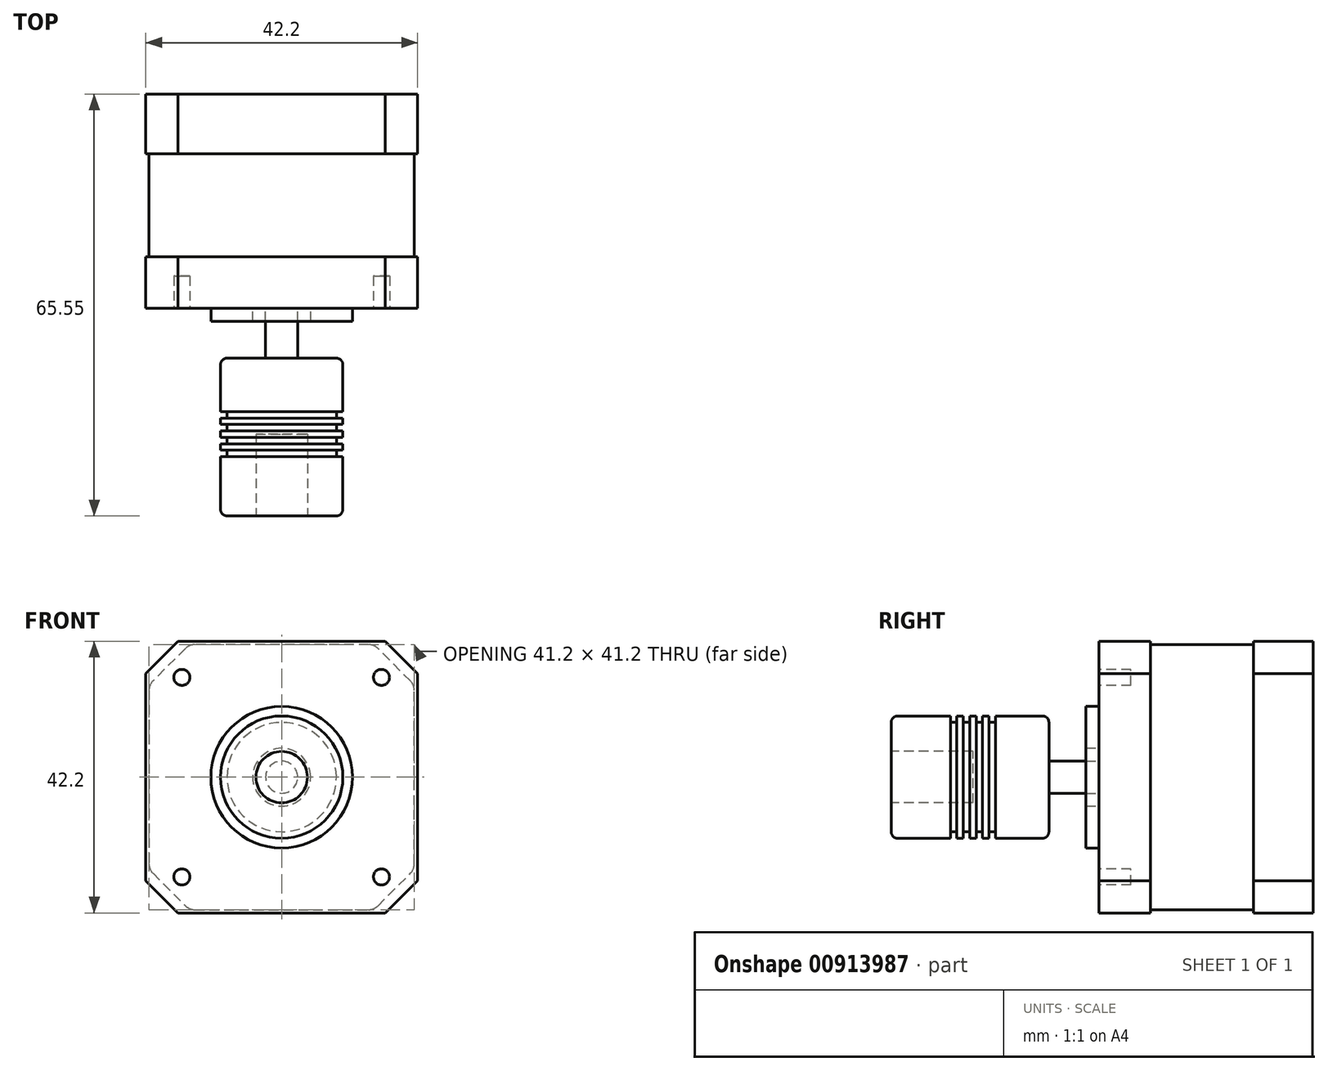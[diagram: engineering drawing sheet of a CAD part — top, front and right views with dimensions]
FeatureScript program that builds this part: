
annotation { "Feature Type Name" : "Feature", "Feature Type Description" : "" }
export const myFeature = defineFeature(function(context is Context, id is Id, definition is map)
    precondition{}
    {
        {
            var Q0;
            Q0=qCreatedBy(makeId("Front.planeOp"),FACE);
            var sketch = newSketch(context, id + "F0", { "sketchPlane" : qUnion([Q0])});
            skLineSegment(sketch, "E0.bottom", {"start": v(-21.1, 21.1) * mm, "end": v(21.1, 21.1) * mm});
            skLineSegment(sketch, "E0.top", {"start": v(-21.1, -21.1) * mm, "end": v(21.1, -21.1) * mm});
            skLineSegment(sketch, "E0.left", {"start": v(-21.1, 21.1) * mm, "end": v(-21.1, -21.1) * mm});
            skLineSegment(sketch, "E0.right", {"start": v(21.1, 21.1) * mm, "end": v(21.1, -21.1) * mm});
            skLineSegment(sketch, "E1", {"start": v(-21.1, 21.1) * mm, "end": v(21.1, -21.1) * mm, "construction": true});
            skCircle(sketch, "E2", {"center": v(0, 0) * mm, "radius": 2.5 * mm});
            skSolve(sketch);
        }
        {
            var Q0;
            Q0=makeQuery(id+"F0.imprint","IMPRINT",FACE,{"disambiguationData":[TD([[makeQuery(id+"F0.imprint","IMPRINT",EDGE,{"derivedFrom":sQuery(id+"F0.wireOp",EDGE,"E2")}),1.0]])]});
            var Q1;
            Q1=makeQuery(id+"F0.imprint","IMPRINT",FACE,{"disambiguationData":[TD([[makeQuery(id+"F0.imprint","IMPRINT",EDGE,{"derivedFrom":sQuery(id+"F0.wireOp",EDGE,"E0.bottom")}),-1.0]])]});
            extrude(context, id + "F1", {"entities" : qUnion([Q0, Q1]), "oppositeDirection" : true, "depth" : 33.3 * mm, "offsetDistance" : 25 * mm});
        }
        {
            var Q0;
            Q0=makeQuery(id+"F1.opExtrude","SWEPT_EDGE",EDGE,{"disambiguationData":[OSD([sQuery(id+"F0.wireOp",EDGE,"E0.bottom"),sQuery(id+"F0.wireOp",EDGE,"E0.right")])]});
            var Q1;
            Q1=makeQuery(id+"F1.opExtrude","SWEPT_EDGE",EDGE,{"disambiguationData":[OSD([sQuery(id+"F0.wireOp",EDGE,"E0.bottom"),sQuery(id+"F0.wireOp",EDGE,"E0.left")])]});
            var Q2;
            Q2=makeQuery(id+"F1.opExtrude","SWEPT_EDGE",EDGE,{"disambiguationData":[OSD([sQuery(id+"F0.wireOp",EDGE,"E0.top"),sQuery(id+"F0.wireOp",EDGE,"E0.right")])]});
            var Q3;
            Q3=makeQuery(id+"F1.opExtrude","SWEPT_EDGE",EDGE,{"disambiguationData":[OSD([sQuery(id+"F0.wireOp",EDGE,"E0.top"),sQuery(id+"F0.wireOp",EDGE,"E0.left")])]});
            chamfer(context, id + "F2", {"entities" : qUnion([Q0, Q1, Q2, Q3]), "width" : 5 * mm, "tangentPropagation" : true});
        }
        {
            var Q0;
            Q0=makeQuery(id+"F0.imprint","IMPRINT",FACE,{"disambiguationData":[TD([[makeQuery(id+"F0.imprint","IMPRINT",EDGE,{"derivedFrom":sQuery(id+"F0.wireOp",EDGE,"E2")}),1.0]])]});
            extrude(context, id + "F3", {"entities" : qUnion([Q0]), "operationType" : NewBodyOperationType.ADD, "depth" : 20 * mm, "offsetDistance" : 25 * mm});
        }
        {
            var Q0;
            Q0=makeQuery(id+"F1.opExtrude","CAP_FACE",FACE,{"disambiguationData":[OSD([sQuery(id+"F0.wireOp",EDGE,"E0.bottom"),sQuery(id+"F0.wireOp",EDGE,"E0.top"),sQuery(id+"F0.wireOp",EDGE,"E0.left"),sQuery(id+"F0.wireOp",EDGE,"E0.right")])],"isStart":true});
            var sketch = newSketch(context, id + "F4", { "sketchPlane" : qUnion([Q0])});
            skCircle(sketch, "E3", {"center": v(0, 0) * mm, "radius": 4.5 * mm});
            skCircle(sketch, "E4", {"center": v(0, 0) * mm, "radius": 11 * mm});
            skSolve(sketch);
        }
        {
            var Q0;
            Q0=qSketchRegion(id+"F4",true);
            extrude(context, id + "F5", {"entities" : qUnion([Q0]), "operationType" : NewBodyOperationType.ADD, "depth" : 2 * mm, "offsetDistance" : 25 * mm});
        }
        {
            var Q0;
            {var subQ0=sQuery(id+"F0.wireOp",EDGE,"E0.left");var subQ1=sQuery(id+"F0.wireOp",EDGE,"E0.bottom");var subQ2=sQuery(id+"F0.wireOp",EDGE,"E0.top");var subQ3=sQuery(id+"F0.wireOp",EDGE,"E0.right");Q0=makeQuery(id+"F5.boolean.opBoolean","SPLIT",FACE,{"disambiguationData":[TD([makeQuery(id+"F1.opExtrude","SWEPT_FACE",FACE,{"disambiguationData":[OSD([subQ1])]})])],"derivedFrom":makeQuery(id+"F1.opExtrude","CAP_FACE",FACE,{"disambiguationData":[OSD([subQ1,subQ2,subQ0,subQ3])],"isStart":true})});}
            var sketch = newSketch(context, id + "F6", { "sketchPlane" : qUnion([Q0])});
            skCircle(sketch, "E5", {"center": v(-15.5, 15.5) * mm, "radius": 1.25 * mm});
            skCircle(sketch, "E6.1.0", {"center": v(-15.5, -15.5) * mm, "radius": 1.25 * mm});
            skCircle(sketch, "E6.2.0", {"center": v(15.5, -15.5) * mm, "radius": 1.25 * mm});
            skCircle(sketch, "E6.3.0", {"center": v(15.5, 15.5) * mm, "radius": 1.25 * mm});
            skPoint(sketch, "E6.center", {"position": v(0, 0) * mm});
            skSolve(sketch);
        }
        {
            var Q0;
            Q0=qSketchRegion(id+"F6",true);
            extrude(context, id + "F7", {"entities" : qUnion([Q0]), "operationType" : NewBodyOperationType.REMOVE, "oppositeDirection" : true, "depth" : 5 * mm, "offsetDistance" : 25 * mm});
        }
        {
            var Q0;
            {var subQ0=sQuery(id+"F0.wireOp",EDGE,"E0.left");var subQ1=sQuery(id+"F0.wireOp",EDGE,"E0.bottom");var subQ2=sQuery(id+"F0.wireOp",EDGE,"E0.top");var subQ3=sQuery(id+"F0.wireOp",EDGE,"E0.right");Q0=makeQuery(id+"F5.boolean.opBoolean","SPLIT",FACE,{"disambiguationData":[TD([makeQuery(id+"F1.opExtrude","SWEPT_FACE",FACE,{"disambiguationData":[OSD([subQ1])]})])],"derivedFrom":makeQuery(id+"F1.opExtrude","CAP_FACE",FACE,{"disambiguationData":[OSD([subQ1,subQ2,subQ0,subQ3])],"isStart":true})});}
            cPlane(context, id + "F8", {"entities" : qUnion([Q0]), "cplaneType" : CPlaneType.OFFSET, "offset" : 8 * mm, "oppositeDirection" : true, "width" : 150 * mm, "height" : 150 * mm});
        }
        {
            var Q0;
            Q0=qCreatedBy(id+"F8.planeOp",FACE);
            var sketch = newSketch(context, id + "F9", { "sketchPlane" : qUnion([Q0])});
            skLineSegment(sketch, "E7", {"start": v(0, 0) * mm, "end": v(0, 20.6) * mm});
            skLineSegment(sketch, "E8", {"start": v(0, 20.6) * mm, "end": v(-14.34, 20.6) * mm});
            skLineSegment(sketch, "E9", {"start": v(-14.34, 20.6) * mm, "end": v(-20.6, 14.34) * mm});
            skLineSegment(sketch, "E10", {"start": v(-20.6, 14.34) * mm, "end": v(-20.6, 0) * mm});
            skLineSegment(sketch, "E11", {"start": v(-20.6, 0) * mm, "end": v(0, 0) * mm});
            skLineSegment(sketch, "E12.1.0", {"start": v(-20.6, 0) * mm, "end": v(-20.6, -14.34) * mm});
            skLineSegment(sketch, "E12.1.1", {"start": v(-14.34, -20.6) * mm, "end": v(0, -20.6) * mm});
            skLineSegment(sketch, "E12.1.2", {"start": v(-20.6, -14.34) * mm, "end": v(-14.34, -20.6) * mm});
            skLineSegment(sketch, "E12.2.0", {"start": v(0, -20.6) * mm, "end": v(14.34, -20.6) * mm});
            skLineSegment(sketch, "E12.2.1", {"start": v(20.6, -14.34) * mm, "end": v(20.6, 0) * mm});
            skLineSegment(sketch, "E12.2.2", {"start": v(14.34, -20.6) * mm, "end": v(20.6, -14.34) * mm});
            skLineSegment(sketch, "E12.3.0", {"start": v(20.6, 0) * mm, "end": v(20.6, 14.34) * mm});
            skLineSegment(sketch, "E12.3.1", {"start": v(14.34, 20.6) * mm, "end": v(0, 20.6) * mm});
            skLineSegment(sketch, "E12.3.2", {"start": v(20.6, 14.34) * mm, "end": v(14.34, 20.6) * mm});
            skPoint(sketch, "E12.center", {"position": v(0, 0) * mm});
            skLineSegment(sketch, "E13.bottom", {"start": v(-24.85, 25.17) * mm, "end": v(25.9, 25.17) * mm});
            skLineSegment(sketch, "E13.top", {"start": v(-24.85, -25.03) * mm, "end": v(25.9, -25.03) * mm});
            skLineSegment(sketch, "E13.left", {"start": v(-24.85, 25.17) * mm, "end": v(-24.85, -25.03) * mm});
            skLineSegment(sketch, "E13.right", {"start": v(25.9, 25.17) * mm, "end": v(25.9, -25.03) * mm});
            skSolve(sketch);
        }
        {
            var Q0;
            Q0=qSketchRegion(id+"F9",true);
            extrude(context, id + "F10", {"entities" : qUnion([Q0]), "operationType" : NewBodyOperationType.REMOVE, "oppositeDirection" : true, "depth" : 16 * mm, "offsetDistance" : 25 * mm});
        }
        {
            var Q0;
            Q0=makeQuery(id+"F10.boolean.opBoolean","COPY",EDGE,{"derivedFrom":makeQuery(id+"F10.opExtrude","SWEPT_EDGE",EDGE,{"disambiguationData":[OSD([sQuery(id+"F9.wireOp",EDGE,"E12.3.0"),sQuery(id+"F9.wireOp",EDGE,"E12.3.2")])]})});
            var Q1;
            Q1=makeQuery(id+"F10.boolean.opBoolean","COPY",EDGE,{"derivedFrom":makeQuery(id+"F10.opExtrude","SWEPT_EDGE",EDGE,{"disambiguationData":[OSD([sQuery(id+"F9.wireOp",EDGE,"E12.3.1"),sQuery(id+"F9.wireOp",EDGE,"E12.3.2")])]})});
            var Q2;
            Q2=makeQuery(id+"F10.boolean.opBoolean","COPY",EDGE,{"derivedFrom":makeQuery(id+"F10.opExtrude","SWEPT_EDGE",EDGE,{"disambiguationData":[OSD([sQuery(id+"F9.wireOp",EDGE,"E8"),sQuery(id+"F9.wireOp",EDGE,"E9")])]})});
            var Q3;
            Q3=makeQuery(id+"F10.boolean.opBoolean","COPY",EDGE,{"derivedFrom":makeQuery(id+"F10.opExtrude","SWEPT_EDGE",EDGE,{"disambiguationData":[OSD([sQuery(id+"F9.wireOp",EDGE,"E9"),sQuery(id+"F9.wireOp",EDGE,"E10")])]})});
            var Q4;
            Q4=makeQuery(id+"F10.boolean.opBoolean","COPY",EDGE,{"derivedFrom":makeQuery(id+"F10.opExtrude","SWEPT_EDGE",EDGE,{"disambiguationData":[OSD([sQuery(id+"F9.wireOp",EDGE,"E12.1.0"),sQuery(id+"F9.wireOp",EDGE,"E12.1.2")])]})});
            var Q5;
            Q5=makeQuery(id+"F10.boolean.opBoolean","COPY",EDGE,{"derivedFrom":makeQuery(id+"F10.opExtrude","SWEPT_EDGE",EDGE,{"disambiguationData":[OSD([sQuery(id+"F9.wireOp",EDGE,"E12.1.1"),sQuery(id+"F9.wireOp",EDGE,"E12.1.2")])]})});
            var Q6;
            Q6=makeQuery(id+"F10.boolean.opBoolean","COPY",EDGE,{"derivedFrom":makeQuery(id+"F10.opExtrude","SWEPT_EDGE",EDGE,{"disambiguationData":[OSD([sQuery(id+"F9.wireOp",EDGE,"E12.2.1"),sQuery(id+"F9.wireOp",EDGE,"E12.2.2")])]})});
            var Q7;
            Q7=makeQuery(id+"F10.boolean.opBoolean","COPY",EDGE,{"derivedFrom":makeQuery(id+"F10.opExtrude","SWEPT_EDGE",EDGE,{"disambiguationData":[OSD([sQuery(id+"F9.wireOp",EDGE,"E12.2.0"),sQuery(id+"F9.wireOp",EDGE,"E12.2.2")])]})});
            fillet(context, id + "F11", {"entities" : qUnion([Q0, Q1, Q2, Q3, Q4, Q5, Q6, Q7]), "radius" : 2 * mm, "tangentPropagation" : true, "allowEdgeOverflow" : false});
        }
        {
            var Q0;
            Q0=makeQuery(id+"F3.opExtrude","CAP_FACE",FACE,{"disambiguationData":[OSD([sQuery(id+"F0.wireOp",EDGE,"E2")])],"isStart":false});
            var sketch = newSketch(context, id + "F12", { "sketchPlane" : qUnion([Q0])});
            skCircle(sketch, "E14", {"center": v(0, 0) * mm, "radius": 9.5 * mm});
            skSolve(sketch);
        }
        {
            var Q0;
            Q0=qSketchRegion(id+"F12",true);
            extrude(context, id + "F13", {"entities" : qUnion([Q0]), "operationType" : NewBodyOperationType.ADD, "endBound" : BoundingType.SYMMETRIC, "depth" : 24.5 * mm, "offsetDistance" : 25 * mm});
        }
        {
            var Q0;
            Q0=makeQuery(id+"F13.opExtrude","CAP_FACE",FACE,{"disambiguationData":[OSD([sQuery(id+"F12.wireOp",EDGE,"E14")])],"isStart":false});
            var sketch = newSketch(context, id + "F14", { "sketchPlane" : qUnion([Q0])});
            skCircle(sketch, "E15", {"center": v(0, 0) * mm, "radius": 4 * mm});
            skSolve(sketch);
        }
        {
            var Q0;
            Q0=qSketchRegion(id+"F14",true);
            extrude(context, id + "F15", {"entities" : qUnion([Q0]), "operationType" : NewBodyOperationType.REMOVE, "oppositeDirection" : true, "depth" : (25.4 / 2) * mm, "offsetDistance" : 25 * mm});
        }
        {
            var Q0;
            Q0=makeQuery(id+"F13.opExtrude","CAP_EDGE",EDGE,{"disambiguationData":[OSD([sQuery(id+"F12.wireOp",EDGE,"E14")])],"isStart":false});
            var Q1;
            Q1=makeQuery(id+"F13.opExtrude","CAP_EDGE",EDGE,{"disambiguationData":[OSD([sQuery(id+"F12.wireOp",EDGE,"E14")])],"isStart":true});
            var Q2;
            Q2=makeQuery(id+"F15.boolean.opBoolean","COPY",EDGE,{"derivedFrom":makeQuery(id+"F15.opExtrude","CAP_EDGE",EDGE,{"disambiguationData":[OSD([sQuery(id+"F14.wireOp",EDGE,"E15")])],"isStart":true})});
            fillet(context, id + "F16", {"entities" : qUnion([Q0, Q1, Q2]), "radius" : 1 * mm, "tangentPropagation" : true, "allowEdgeOverflow" : false});
        }
        {
            var Q0;
            Q0=qCreatedBy(makeId("Right.planeOp"),FACE);
            var sketch = newSketch(context, id + "F17", { "sketchPlane" : qUnion([Q0])});
            skLineSegment(sketch, "E16", {"start": v(-19.55, 17.45) * mm, "end": v(-19.55, -14.9) * mm, "construction": true});
            skLineSegment(sketch, "E17.0", {"start": v(-19.55, -4) * mm, "end": v(-19.55, 4) * mm, "construction": true});
            skLineSegment(sketch, "E18", {"start": v(-31.25, 9.5) * mm, "end": v(-8.75, 9.5) * mm});
            skLineSegment(sketch, "E19.bottom", {"start": v(-20.05, 9.5) * mm, "end": v(-21.05, 9.5) * mm});
            skLineSegment(sketch, "E19.top", {"start": v(-20.05, 8.5) * mm, "end": v(-21.05, 8.5) * mm});
            skLineSegment(sketch, "E19.left", {"start": v(-20.05, 9.5) * mm, "end": v(-20.05, 8.5) * mm});
            skLineSegment(sketch, "E19.right", {"start": v(-21.05, 9.5) * mm, "end": v(-21.05, 8.5) * mm});
            skLineSegment(sketch, "E20.bottom", {"start": v(-22.05, 9.5) * mm, "end": v(-23.05, 9.5) * mm});
            skLineSegment(sketch, "E20.top", {"start": v(-22.05, 8.5) * mm, "end": v(-23.05, 8.5) * mm});
            skLineSegment(sketch, "E20.left", {"start": v(-22.05, 9.5) * mm, "end": v(-22.05, 8.5) * mm});
            skLineSegment(sketch, "E20.right", {"start": v(-23.05, 9.5) * mm, "end": v(-23.05, 8.5) * mm});
            skLineSegment(sketch, "E21.bottom", {"start": v(-19.05, 9.5) * mm, "end": v(-18.05, 9.5) * mm});
            skLineSegment(sketch, "E21.top", {"start": v(-19.05, 8.5) * mm, "end": v(-18.05, 8.5) * mm});
            skLineSegment(sketch, "E21.left", {"start": v(-19.05, 9.5) * mm, "end": v(-19.05, 8.5) * mm});
            skLineSegment(sketch, "E21.right", {"start": v(-18.05, 9.5) * mm, "end": v(-18.05, 8.5) * mm});
            skLineSegment(sketch, "E22.bottom", {"start": v(-17.05, 9.5) * mm, "end": v(-16.05, 9.5) * mm});
            skLineSegment(sketch, "E22.top", {"start": v(-17.05, 8.5) * mm, "end": v(-16.05, 8.5) * mm});
            skLineSegment(sketch, "E22.left", {"start": v(-17.05, 9.5) * mm, "end": v(-17.05, 8.5) * mm});
            skLineSegment(sketch, "E22.right", {"start": v(-16.05, 9.5) * mm, "end": v(-16.05, 8.5) * mm});
            skLineSegment(sketch, "E23", {"start": v(-19.05, 8.5) * mm, "end": v(-20.05, 8.5) * mm, "construction": true});
            skPoint(sketch, "E24", {"position": v(-19.55, 8.5) * mm});
            skLineSegment(sketch, "E25", {"start": v(-22.05, 8.5) * mm, "end": v(-21.05, 8.5) * mm, "construction": true});
            skLineSegment(sketch, "E26", {"start": v(-18.05, 8.5) * mm, "end": v(-17.05, 8.5) * mm, "construction": true});
            skLineSegment(sketch, "E27", {"start": v(-35.6, 0) * mm, "end": v(18.11, 0) * mm, "construction": true});
            skSolve(sketch);
        }
        {
            var Q0;
            Q0=qSketchRegion(id+"F17",true);
            var Q1;
            Q1=sQuery(id+"F17.wireOp",EDGE,"E27");
            revolve(context, id + "F18", {"operationType" : NewBodyOperationType.REMOVE, "surfaceOperationType" : NewSurfaceOperationType.NEW, "entities" : qUnion([Q0]), "axis" : qUnion([Q1]), "revolveType" : RevolveType.FULL, "oppositeDirection" : true});
        }
    });
